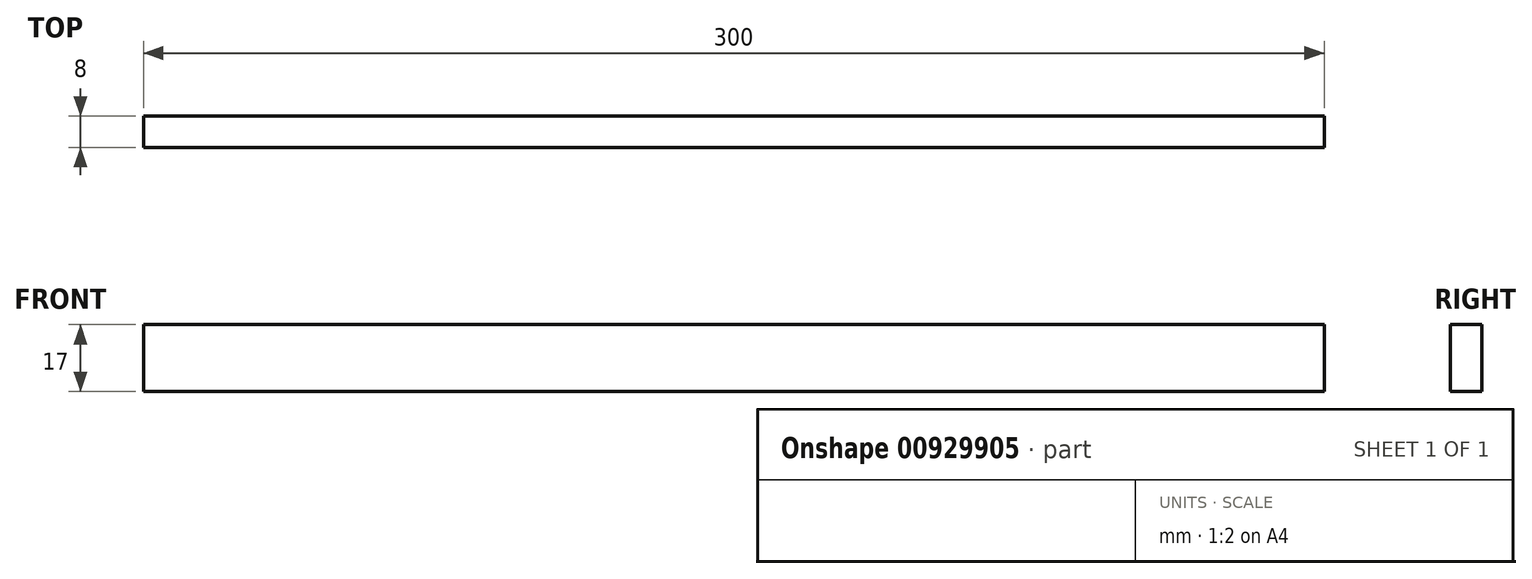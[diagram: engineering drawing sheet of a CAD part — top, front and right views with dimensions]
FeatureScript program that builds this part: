
annotation { "Feature Type Name" : "Feature", "Feature Type Description" : "" }
export const myFeature = defineFeature(function(context is Context, id is Id, definition is map)
    precondition{}
    {
        {
            var Q0;
            Q0=qCreatedBy(makeId("Front.planeOp"),FACE);
            var sketch = newSketch(context, id + "F0", { "sketchPlane" : qUnion([Q0])});
            skLineSegment(sketch, "E0.bottom", {"start": v(0, 0) * mm, "end": v(300, 0) * mm});
            skLineSegment(sketch, "E0.top", {"start": v(0, 17) * mm, "end": v(300, 17) * mm});
            skLineSegment(sketch, "E0.left", {"start": v(0, 0) * mm, "end": v(0, 17) * mm});
            skLineSegment(sketch, "E0.right", {"start": v(300, 0) * mm, "end": v(300, 17) * mm});
            skSolve(sketch);
        }
        {
            var Q0;
            Q0 = qSketchRegion(id + "F0", true);
            extrude(context, id + "F1", {"entities" : qUnion([Q0]), "depth" : 8 * mm, "offsetDistance" : 25 * mm});
        }
    });
